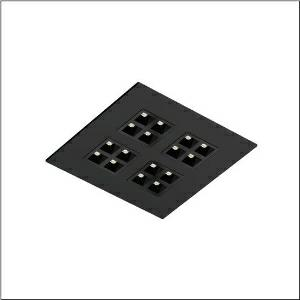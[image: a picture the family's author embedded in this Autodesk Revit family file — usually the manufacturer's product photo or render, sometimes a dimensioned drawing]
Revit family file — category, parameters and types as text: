
# Revit family: silica_31_square_51my6lds44ba
name_source: partatom
category: Lighting Fixtures
units: mm (PartAtom-declared; Revit-internal decimal feet)

## family parameters
Cut with Voids When Loaded = No
Host = Face
Light Source = No
Part Type = Normal
Room Calculation Point = No
Round Connector Dimension = Use Diameter
Shared = No

## types (1)
- --- (1 x LED, 6310 lm, 38.5 W, 4000K)
    Apparent Load = 39 VA
    CIE Flux Codes = 82 100 100 100 100
    Color Rendering = 80
    Color Temperature = 4000K
    Default Elevation = 1800 mm
    Description = Silica 31 Square, office luminaire, primary light control with lens, of PMMA, primary anti-glare with reflector, of PC, black, light emission: direct distribution, primary light characteristic: symmetric, installation type: lay-in mounting, LED, rated luminous flux: 4.620lm, luminous efficacy: 167lm/W, light colour: 840, colour temperature: 4000K, control gear: DALI 2, Multilumen, with terminal, 5-pole, mains connection: 220..240V, AC, 50/60Hz, rated input power: 27.6W, luminaire housing, of sheet steel, coated, jet black (RAL 9005), module: M600, length: 595mm, width: 595mm, height: 43mm, protection rating (complete): IP20, insulation class (complete): insulation class II (safety insulation), certification: CE, impact resistance: IK03, permissible operating ambient temperature: -20..+35°C, standard: EN 50419, packaging unit: 1 piece
    Height = 0 mm  [stored 0 ft]
    Lamp = 1 x LED
    Lamp Light Flux = 6310 lm
    Lamp Power = 38.5 W
    Lamp count = 1
    Length = 595 mm
    Luminous efficacy = 164 lm/W
    Manufacturer = Siteco
    ModVariant = No
    Model = 51MY6LDS44BA
    Mounting Place = Ceiling
    Mounting Type = Recessed
    Number of Poles = 1
    OnlyDefault = Yes
    Power Factor = 1
    Product Name = Silica 31 Square
    Product group = office luminaire | ceiling recessed
    ProductGroupID = 400
    Protection Class = Protection class II
    Protection Degree = IP 20
    RLX_Detail_Level = 1
    RLX_Emergency_Light_Flux = 0 lm
    RLX_Emergency_Type = 0
    RLX_Emergency_Type_DB = No
    RlxData = <blob elided: 35525 chars, md5=29a95bca>
    Socket = socket
    Standby Power = 0 W
    System Light Flux = 6310 lm
    System Power = 39 W
    Type Comments = factory setting: luminous flux: 100 % | (OFF | OFF | OFF | OFF) | 1050 mA
    Type Image = l_1313660.jpg
    URL = http://relux.com
    VarID = @adj_043229
    Voltage = 0 V
    Weight = 0.00 kg
    Width = 595 mm

note: [stored X ft] marks values corroborated as IEEE doubles in the binary element streams (Revit-internal decimal feet)

## geometry (parser evidence)
native form markers: Blend x4, Sweep x11
no freeform markers — native parametric forms only
